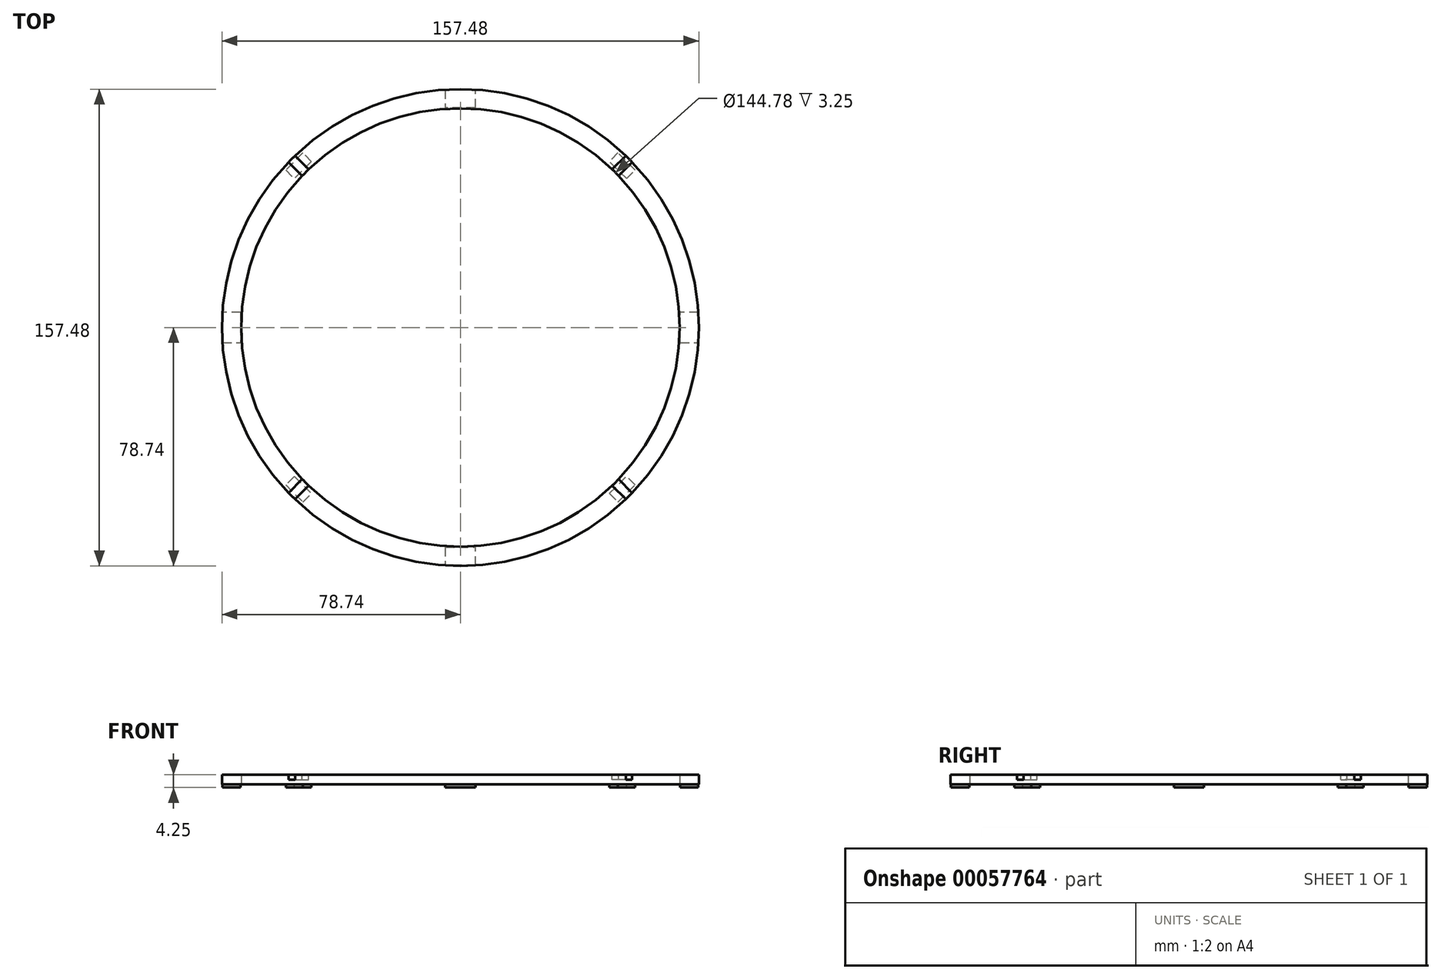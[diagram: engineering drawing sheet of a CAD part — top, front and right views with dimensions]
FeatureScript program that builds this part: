
annotation { "Feature Type Name" : "Feature", "Feature Type Description" : "" }
export const myFeature = defineFeature(function(context is Context, id is Id, definition is map)
    precondition{}
    {
        {
            var Q0;
            Q0=qCreatedBy(makeId("Top.planeOp"),FACE);
            var sketch = newSketch(context, id + "F0", { "sketchPlane" : qUnion([Q0])});
            skCircle(sketch, "E0", {"center": v(0, 0) * mm, "radius": 78.74 * mm});
            skCircle(sketch, "E1", {"center": v(0, 0) * mm, "radius": 72.39 * mm});
            skSolve(sketch);
        }
        {
            var Q0;
            Q0 = qSketchRegion(id + "F0", true);
            extrude(context, id + "F1", {"entities" : qUnion([Q0]), "depth" : 3.25 * mm});
        }
        {
            var Q0;
            Q0=makeQuery(id+"F1.opExtrude","CAP_FACE",FACE,{"disambiguationData":[OSD([sQuery(id+"F0.wireOp",EDGE,"E0"),sQuery(id+"F0.wireOp",EDGE,"E1")])],"isStart":false});
            var sketch = newSketch(context, id + "F2", { "sketchPlane" : qUnion([Q0])});
            skLineSegment(sketch, "E2", {"start": v(0, 0) * mm, "end": v(-72.14, 72.14) * mm, "construction": true});
            skLineSegment(sketch, "E3", {"start": v(0, 0) * mm, "end": v(0, 87.95) * mm, "construction": true});
            skLineSegment(sketch, "E4", {"start": v(-54.6, 56.73) * mm, "end": v(-50.12, 52.24) * mm});
            skLineSegment(sketch, "E5.MirrorCS", {"start": v(-56.73, 54.6) * mm, "end": v(-52.24, 50.12) * mm});
            skSolve(sketch);
        }
        {
            var Q0;
            {var subQ0=sQuery(id+"F2.wireOp",EDGE,"E4");Q0=makeQuery(id+"F2.imprint","IMPRINT",FACE,{"disambiguationData":[TD([[makeQuery(id+"F2.imprint","IMPRINT",EDGE,{"derivedFrom":subQ0}),-1.0]])]});}
            extrude(context, id + "F3", {"entities" : qUnion([Q0]), "operationType" : NewBodyOperationType.REMOVE, "oppositeDirection" : true, "depth" : 1.63 * mm});
        }
        {
            var Q0;
            Q0=makeQuery(id+"F1.opExtrude","SWEPT_BODY",BODY,{"disambiguationData":[OSD([sQuery(id+"F0.wireOp",EDGE,"E0"),sQuery(id+"F0.wireOp",EDGE,"E1")])]});
            var Q1;
            Q1=makeQuery(id+"F3.boolean.opBoolean","COPY",FACE,{"derivedFrom":makeQuery(id+"F3.opExtrude","CAP_FACE",FACE,{"disambiguationData":[OSD([sQuery(id+"F0.wireOp",EDGE,"E0"),sQuery(id+"F0.wireOp",EDGE,"E1"),sQuery(id+"F2.wireOp",EDGE,"E4"),sQuery(id+"F2.wireOp",EDGE,"E5.MirrorCS")])],"isStart":false})});
            var Q2;
            Q2=makeQuery(id+"F3.boolean.opBoolean","COPY",FACE,{"derivedFrom":makeQuery(id+"F3.opExtrude","SWEPT_FACE",FACE,{"disambiguationData":[OSD([sQuery(id+"F2.wireOp",EDGE,"E4")])]})});
            var Q3;
            Q3=makeQuery(id+"F3.boolean.opBoolean","COPY",FACE,{"derivedFrom":makeQuery(id+"F3.opExtrude","SWEPT_FACE",FACE,{"disambiguationData":[OSD([sQuery(id+"F2.wireOp",EDGE,"E5.MirrorCS")])]})});
            var Q4;
            Q4=makeQuery(id+"F1.opExtrude","SWEPT_FACE",FACE,{"disambiguationData":[OSD([sQuery(id+"F0.wireOp",EDGE,"E1")])]});
            circularPattern(context, id + "F4", {"faces" : qUnion([Q1, Q2, Q3]), "axis" : qUnion([Q4]), "angle" : 90 * degree, "instanceCount" : 4, "patternType" : PatternType.FACE});
        }
        {
            var Q0;
            Q0=makeQuery(id+"F1.opExtrude","CAP_FACE",FACE,{"disambiguationData":[OSD([sQuery(id+"F0.wireOp",EDGE,"E0"),sQuery(id+"F0.wireOp",EDGE,"E1")])],"isStart":true});
            var sketch = newSketch(context, id + "F5", { "sketchPlane" : qUnion([Q0])});
            skLineSegment(sketch, "E6", {"start": v(0, 0) * mm, "end": v(-66.74, 66.74) * mm, "construction": true});
            skLineSegment(sketch, "E7", {"start": v(0, 0) * mm, "end": v(0, 82.68) * mm, "construction": true});
            skLineSegment(sketch, "E8", {"start": v(-51.19, 51.19) * mm, "end": v(-55.68, 55.68) * mm});
            skPoint(sketch, "E9.rect.middle", {"position": v(-53.43, 53.43) * mm});
            skLineSegment(sketch, "E10", {"start": v(-50.6, 56.26) * mm, "end": v(-52.02, 57.68) * mm});
            skLineSegment(sketch, "E11", {"start": v(-52.02, 57.68) * mm, "end": v(-54.85, 54.85) * mm});
            skLineSegment(sketch, "E12.MirrorCS", {"start": v(-49.19, 54.85) * mm, "end": v(-52.02, 52.02) * mm});
            skLineSegment(sketch, "E13.MirrorCS", {"start": v(-50.6, 56.26) * mm, "end": v(-49.19, 54.85) * mm});
            skLineSegment(sketch, "E14.MirrorCS", {"start": v(-57.68, 52.02) * mm, "end": v(-54.85, 54.85) * mm});
            skLineSegment(sketch, "E15.MirrorCS", {"start": v(-56.26, 50.6) * mm, "end": v(-57.68, 52.02) * mm});
            skLineSegment(sketch, "E16.MirrorCS", {"start": v(-56.26, 50.6) * mm, "end": v(-54.85, 49.19) * mm});
            skLineSegment(sketch, "E17.MirrorCS", {"start": v(-54.85, 49.19) * mm, "end": v(-52.02, 52.02) * mm});
            skSolve(sketch);
        }
        {
            var Q0;
            {var subQ0=sQuery(id+"F5.wireOp",EDGE,"E14.MirrorCS");Q0=makeQuery(id+"F5.imprint","IMPRINT",FACE,{"disambiguationData":[TD([[makeQuery(id+"F5.imprint","IMPRINT",EDGE,{"derivedFrom":subQ0}),-1.0]])]});}
            var Q1;
            Q1=makeQuery(id+"F5.imprint","IMPRINT",FACE,{"disambiguationData":[TD([[makeQuery(id+"F5.imprint","IMPRINT",EDGE,{"derivedFrom":sQuery(id+"F5.wireOp",EDGE,"E10")}),1.0]])]});
            extrude(context, id + "F6", {"entities" : qUnion([Q0, Q1]), "operationType" : NewBodyOperationType.ADD, "depth" : 1 * mm});
        }
        {
            var Q0;
            Q0=makeQuery(id+"F6.opExtrude","CAP_FACE",FACE,{"disambiguationData":[OSD([sQuery(id+"F5.wireOp",EDGE,"E10"),sQuery(id+"F5.wireOp",EDGE,"E11"),sQuery(id+"F5.wireOp",EDGE,"E12.MirrorCS"),sQuery(id+"F5.wireOp",EDGE,"E13.MirrorCS"),sQuery(id+"F5.wireOp",EDGE,"E14.MirrorCS"),sQuery(id+"F5.wireOp",EDGE,"E15.MirrorCS"),sQuery(id+"F5.wireOp",EDGE,"E16.MirrorCS"),sQuery(id+"F5.wireOp",EDGE,"E17.MirrorCS")])],"isStart":false});
            var Q1;
            Q1=makeQuery(id+"F6.opExtrude","SWEPT_FACE",FACE,{"disambiguationData":[OSD([sQuery(id+"F5.wireOp",EDGE,"E12.MirrorCS"),sQuery(id+"F5.wireOp",EDGE,"E17.MirrorCS")])]});
            var Q2;
            Q2=makeQuery(id+"F6.opExtrude","SWEPT_FACE",FACE,{"disambiguationData":[OSD([sQuery(id+"F5.wireOp",EDGE,"E11"),sQuery(id+"F5.wireOp",EDGE,"E14.MirrorCS")])]});
            var Q3;
            Q3=makeQuery(id+"F6.opExtrude","SWEPT_FACE",FACE,{"disambiguationData":[OSD([sQuery(id+"F5.wireOp",EDGE,"E10"),sQuery(id+"F5.wireOp",EDGE,"E13.MirrorCS")])]});
            var Q4;
            Q4=makeQuery(id+"F6.opExtrude","SWEPT_FACE",FACE,{"disambiguationData":[OSD([sQuery(id+"F5.wireOp",EDGE,"E15.MirrorCS"),sQuery(id+"F5.wireOp",EDGE,"E16.MirrorCS")])]});
            var Q5;
            Q5=makeQuery(id+"F1.opExtrude","SWEPT_FACE",FACE,{"disambiguationData":[OSD([sQuery(id+"F0.wireOp",EDGE,"E1")])]});
            circularPattern(context, id + "F7", {"faces" : qUnion([Q0, Q1, Q2, Q3, Q4]), "axis" : qUnion([Q5]), "angle" : 90 * degree, "instanceCount" : 4, "patternType" : PatternType.FACE});
        }
        {
            var Q0;
            Q0=makeQuery(id+"F1.opExtrude","CAP_FACE",FACE,{"disambiguationData":[OSD([sQuery(id+"F0.wireOp",EDGE,"E0"),sQuery(id+"F0.wireOp",EDGE,"E1")])],"isStart":true});
            var sketch = newSketch(context, id + "F8", { "sketchPlane" : qUnion([Q0])});
            skLineSegment(sketch, "E18", {"start": v(-5, 75.56) * mm, "end": v(-5, 78.56) * mm});
            skLineSegment(sketch, "E19", {"start": v(-5, 78.56) * mm, "end": v(0, 78.56) * mm});
            skLineSegment(sketch, "E20.MirrorCS", {"start": v(5, 78.56) * mm, "end": v(0, 78.56) * mm});
            skLineSegment(sketch, "E21.MirrorCS", {"start": v(5, 75.56) * mm, "end": v(5, 78.56) * mm});
            skLineSegment(sketch, "E22.MirrorCS", {"start": v(5, 75.56) * mm, "end": v(5, 72.56) * mm});
            skLineSegment(sketch, "E23.MirrorCS", {"start": v(5, 72.56) * mm, "end": v(0, 72.56) * mm});
            skLineSegment(sketch, "E24.MirrorCS", {"start": v(-5, 75.56) * mm, "end": v(-5, 72.56) * mm});
            skLineSegment(sketch, "E25.MirrorCS", {"start": v(-5, 72.56) * mm, "end": v(0, 72.56) * mm});
            skSolve(sketch);
        }
        {
            var Q0;
            Q0=makeQuery(id+"F8.imprint","IMPRINT",FACE,{"disambiguationData":[TD([[makeQuery(id+"F8.imprint","IMPRINT",EDGE,{"derivedFrom":sQuery(id+"F8.wireOp",EDGE,"E18")}),-1.0]])]});
            extrude(context, id + "F9", {"entities" : qUnion([Q0]), "operationType" : NewBodyOperationType.ADD, "depth" : 1 * mm});
        }
        {
            var Q0;
            Q0=makeQuery(id+"F9.opExtrude","CAP_FACE",FACE,{"disambiguationData":[OSD([sQuery(id+"F8.wireOp",EDGE,"E18"),sQuery(id+"F8.wireOp",EDGE,"E19"),sQuery(id+"F8.wireOp",EDGE,"E20.MirrorCS"),sQuery(id+"F8.wireOp",EDGE,"E21.MirrorCS"),sQuery(id+"F8.wireOp",EDGE,"E22.MirrorCS"),sQuery(id+"F8.wireOp",EDGE,"E23.MirrorCS"),sQuery(id+"F8.wireOp",EDGE,"E24.MirrorCS"),sQuery(id+"F8.wireOp",EDGE,"E25.MirrorCS")])],"isStart":false});
            var Q1;
            Q1=makeQuery(id+"F9.opExtrude","SWEPT_FACE",FACE,{"disambiguationData":[OSD([sQuery(id+"F8.wireOp",EDGE,"E19"),sQuery(id+"F8.wireOp",EDGE,"E20.MirrorCS")])]});
            var Q2;
            Q2=makeQuery(id+"F9.opExtrude","SWEPT_FACE",FACE,{"disambiguationData":[OSD([sQuery(id+"F8.wireOp",EDGE,"E18"),sQuery(id+"F8.wireOp",EDGE,"E24.MirrorCS")])]});
            var Q3;
            Q3=makeQuery(id+"F9.opExtrude","SWEPT_FACE",FACE,{"disambiguationData":[OSD([sQuery(id+"F8.wireOp",EDGE,"E21.MirrorCS"),sQuery(id+"F8.wireOp",EDGE,"E22.MirrorCS")])]});
            var Q4;
            Q4=makeQuery(id+"F9.opExtrude","SWEPT_FACE",FACE,{"disambiguationData":[OSD([sQuery(id+"F8.wireOp",EDGE,"E23.MirrorCS"),sQuery(id+"F8.wireOp",EDGE,"E25.MirrorCS")])]});
            var Q5;
            Q5=makeQuery(id+"F1.opExtrude","CAP_EDGE",EDGE,{"disambiguationData":[OSD([sQuery(id+"F0.wireOp",EDGE,"E1")])],"isStart":true});
            circularPattern(context, id + "F10", {"faces" : qUnion([Q0, Q1, Q2, Q3, Q4]), "axis" : qUnion([Q5]), "angle" : 90 * degree, "instanceCount" : 4, "patternType" : PatternType.FACE});
        }
    });
